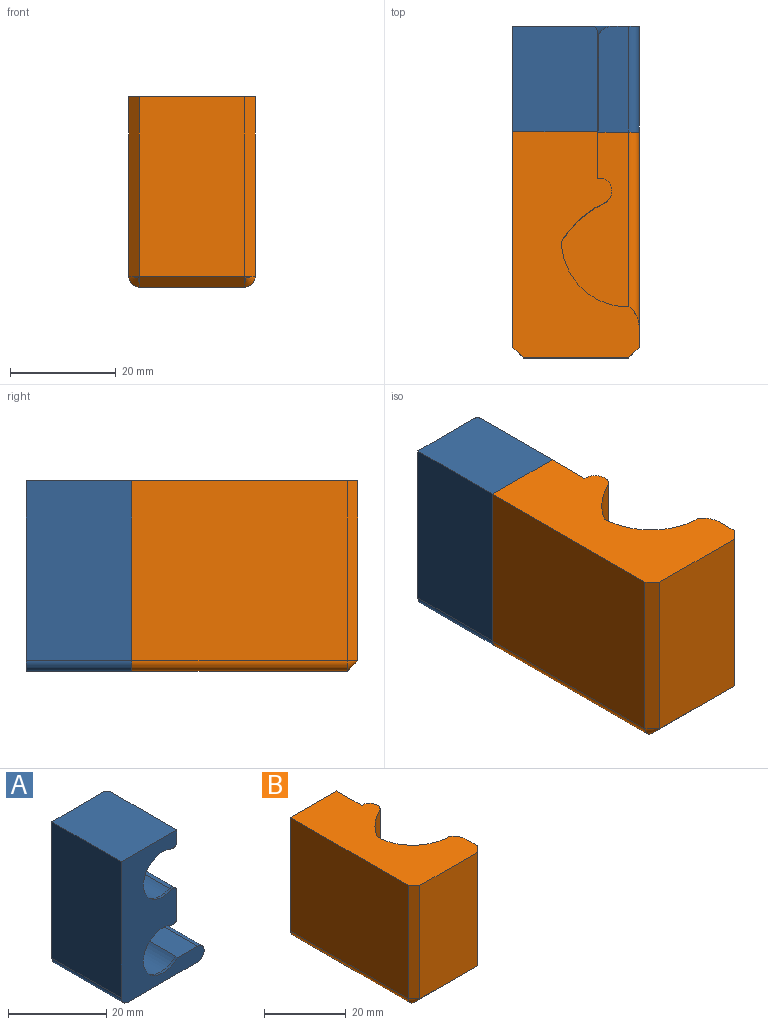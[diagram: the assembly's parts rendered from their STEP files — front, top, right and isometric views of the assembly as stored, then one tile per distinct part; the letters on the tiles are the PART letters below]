
ASSEMBLY  parts=2 mates=1
PART A: 27 faces, bbox 24.2x24.9x39.2 mm
  f0: plane 36x23.89mm, normal (0,1,0), area 286.5mm2, adj f1,f3,f5,f9,f12,f20,f21,f22
  f1: plane 34x20mm, normal (-1,0,0), area 680mm2, adj f0,f2,f20,f26
  f2: plane 36.16x24.05mm, normal (0,-1,0), area 420.7mm2, adj f1,f4,f16,f17,f18,f19,f20,f21
  f3: cylinder r=1mm len=1.92mm, axis (0,0,-1), area 3mm2, adj f0,f4,f7,f26
  f4: plane 19x3.13mm, normal (1,0,0), area 57mm2, adj f2,f3,f7,f15,f16,f26
  f5: torus R=7.75mm, axis (0,1,0), area 81mm2, adj f0,f6,f7,f8
  f6: cylinder r=5.75mm len=17.32mm, axis (0,-1,0), area 402.9mm2, adj f5,f13,f15,f25
  f7: bspline ~3.16x2.62mm, area 5mm2, adj f3,f4,f5,f15
  f8: bspline ~3.16x2.19mm, area 5mm2, adj f5,f9,f13,f19
  f9: cylinder r=1mm len=4.66mm, axis (0,0,-1), area 7.3mm2, adj f0,f8,f10,f19
  f10: bspline ~3.16x2.62mm, area 5mm2, adj f9,f12,f14,f19
  f11: cylinder r=5.75mm len=17.32mm, axis (0,-1,0), area 439.8mm2, adj f12,f14,f22,f24
  f12: torus R=7.75mm, axis (0,1,0), area 91.5mm2, adj f0,f10,f11,f22
  f13: cylinder r=1mm len=17.41mm, axis (0,-1,0), area 35.1mm2, adj f6,f8,f17,f19,f25
  f14: cylinder r=1mm len=17.41mm, axis (0,-1,0), area 35.1mm2, adj f10,f11,f18,f19,f24
  f15: cylinder r=1mm len=17.41mm, axis (0,-1,0), area 35.1mm2, adj f4,f6,f7,f16,f25
  f16: bspline ~7.44x2.95mm, area 1.3mm2, adj f2,f4,f15,f25
  f17: bspline ~7.51x2.96mm, area 1.3mm2, adj f2,f13,f19,f25
  f18: bspline ~6.9x2.95mm, area 1.3mm2, adj f2,f14,f19,f24
  f19: plane 19x7.08mm, normal (1,0,0), area 129.8mm2, adj f2,f8,f9,f10,f13,f14,f17,f18
  f20: cylinder r=2mm len=20mm, axis (0,-1,0), area 62.8mm2, adj f0,f1,f2,f23
  f21: cylinder r=2mm len=20mm, axis (0,1,0), area 125.7mm2, adj f0,f2,f22,f23
  f22: plane 20.36x6.18mm, normal (0,0,1), area 112.2mm2, adj f0,f2,f11,f12,f21,f24
  f23: plane 20x19.89mm, normal (0,0,-1), area 397.8mm2, adj f0,f2,f20,f21
  f24: cone r=5.75mm half-angle=9.7deg, axis (0,1,0), area 17.2mm2, adj f2,f11,f14,f18,f22
  f25: cone r=5.75mm half-angle=9.7deg, axis (0,1,0), area 15.8mm2, adj f2,f6,f13,f15,f16,f17
  f26: plane 20x15.96mm, normal (0,0,1), area 319mm2, adj f0,f1,f2,f3,f4
PART B: 32 faces, bbox 24.6x49.2x36.7 mm
  f0: plane 40.75x34mm, normal (-1,0,0), area 1385.4mm2, adj f1,f29,f30,f31
  f1: plane 34x2mm, normal (-0.71,-0.71,0), area 96.2mm2, adj f0,f2,f28,f31
  f2: cone r=2mm half-angle=45deg, axis (0,1,0), area 4.4mm2, adj f1,f3,f29
  f3: plane 19.89x2mm, normal (0,-0.71,-0.71), area 56.3mm2, adj f2,f4,f27,f28
  f4: cone r=2mm half-angle=45deg, axis (0,1,0), area 4.4mm2, adj f3,f5,f26
  f5: plane 34x2mm, normal (0.71,-0.71,0), area 96.2mm2, adj f4,f6,f28,f31
  f6: plane 34x3.71mm, normal (1,0,0), area 126.2mm2, adj f5,f7,f26,f31
  f7: cylinder r=5mm len=34mm, axis (0,0,1), area 150.7mm2, adj f6,f8,f26,f31
  f8: plane 32x0.07mm, normal (-1,0,0), area 2.2mm2, adj f7,f9,f26,f31
  f9: cylinder r=12.6mm len=32mm, axis (0,0,-1), area 633mm2, adj f8,f10,f25,f26,f31
  f10: cylinder r=19.3mm len=32mm, axis (0,0,-1), area 304.5mm2, adj f9,f11,f20,f21,f23,f24,f25,f31
  f11: cylinder r=1mm len=32mm, axis (0,0,1), area 6.4mm2, adj f10,f12,f25,f31
  f12: cylinder r=2.55mm len=32mm, axis (0,0,-1), area 180.2mm2, adj f11,f13,f25,f31
  f13: plane 32.21x2.76mm, normal (0,1,0), area 34.6mm2, adj f12,f14,f15,f16,f17,f18,f19,f21
  f14: plane 8.77x4.86mm, normal (1,0,0), area 34.9mm2, adj f13,f15,f30,f31
  f15: bspline ~16.03x5.01mm, area 18.6mm2, adj f13,f14,f24,f30
  f16: bspline ~16.12x5.02mm, area 18.6mm2, adj f13,f17,f24,f30
  f17: plane 10.55x8.77mm, normal (1,0,0), area 77mm2, adj f13,f16,f18,f30
  f18: bspline ~14.47x4.87mm, area 18.7mm2, adj f13,f17,f21,f30
  f19: plane 9.04x3.4mm, normal (1,0,0), area 9.7mm2, adj f13,f21,f25
  f20: plane 2.77x0.45mm, normal (0,1,0), area 0.9mm2, adj f10,f21
  f21: cone r=5.75mm half-angle=9.7deg, axis (0,1,0), area 418.3mm2, adj f10,f13,f18,f19,f20,f22,f30
  f22: cone r=5.75mm half-angle=9.7deg, axis (0,1,0), area 0mm2, adj f21,f25,f30
  f23: plane 2.77x0.45mm, normal (0,1,0), area 0.9mm2, adj f10,f24
  f24: cone r=5.75mm half-angle=9.7deg, axis (0,1,0), area 363.4mm2, adj f10,f13,f15,f16,f23,f30
  f25: plane 33.15x12.7mm, normal (0,0,1), area 261mm2, adj f9,f10,f11,f12,f13,f19,f22,f26
  f26: cylinder r=2mm len=40.75mm, axis (0,1,0), area 237.4mm2, adj f4,f6,f7,f8,f9,f25,f27,f30
  f27: plane 40.75x19.89mm, normal (0,0,-1), area 810.4mm2, adj f3,f26,f29,f30
  f28: plane 34x19.89mm, normal (0,-1,0), area 676.2mm2, adj f1,f3,f5,f31
  f29: cylinder r=2mm len=40.75mm, axis (0,-1,0), area 128mm2, adj f0,f2,f27,f30
  f30: plane 36.16x24.05mm, normal (0,1,0), area 420.7mm2, adj f0,f14,f15,f16,f17,f18,f21,f22
  f31: plane 42.75x23.89mm, normal (0,0,1), area 687.6mm2, adj f0,f1,f5,f6,f7,f8,f9,f10
PLACE A t=(-15.85,22.66,-13.7)mm
PLACE B t=(-15.85,22.66,-13.7)mm
MATE fastened A.f2 <-> B.f30  axis (0,-1,0) through (-8.59,21.99,3.43)mm
